# Revit family: is_2360_de_eco_034733
name_source: partatom
category: Elektroinstallationen
revit_build: Autodesk Revit 2016 (Build: 20190508_0715(x64)
units: mm (PartAtom-declared; Revit-internal decimal feet)

## family parameters
Basisbauteil = Fläche
Beim Laden mit Abzugskörper schneiden = Nein
Bemaßung runder Anschluss = Durchmesser verwenden
Beschriftungsausrichtung beibehalten = Nein
Gemeinsam genutzt = Nein
Raumberechnungspunkt = Nein
Teiletyp = Normal

## types (1)
- IS 2360 DE ECO
    Apparent Load = 0 VA
    Beschreibung = Type: Motion detectors; Dimensions (Ø x H): 78 x 84 mm; Mains power supply: 220 – 240 V / 50 – 60 Hz; Sensor Technology: passive infrared; Application, place: Outdoors, Indoors; Application, room: corridor / aisle, changing room, function room / ancillary room, kitchenette, stairwell, WC / washroom, outdoors, front door, all round the building, terrace / balcony, Indoors; Installation site: ceiling; Installation: Installation; Electronic scalability: No; Mechanical scalability: No; Mounting height: 2,2 – 4 m; Optimum mounting height: 2,5 m; Detection angle: 360 °; Angle of aperture: 180 °; Sneak-by guard: Yes; Capability of masking out individual segments: Yes; Reach, radial: Ø 4 m (13 m²); Reach, tangential: Ø 8 m (50 m²); Twilight setting TEACH: No; Twilight setting: 2 – 2000 lx; Time setting: 8 sec – 35 min; Switching output 1, number of LEDs / fluorescent lamps: 6 pcs.; Constant-lighting control: No; Basic light level function: No; Settings via: Potentiometers; Interconnection: No; Type of interconnection: Master/master; IP-rating: IP54; Material: Plastic; Ambient temperature: -20 – 40 °C; Colour: white; Colour, RAL: 9010; IDs, certificates: VDE; Manufacturer's Warranty: 5 years; PU1, EAN: 4007841034733
    Height = 0 mm  [stored 0 ft]
    Hersteller = Steinel
    Length = 78 mm  [stored 0.255906 ft]
    ModVariant = Nein
    Modell = 034733
    Number of Poles = 1
    OnlyDefault = Ja
    Power Factor = 1
    Product Name = IS 2360 DE ECO
    Product group = Sensor-switched indoor light
    ProductGroupID = 30
    Protection Class = Protection class II
    Protection Degree = IP 54
    RlxData = <blob elided: 45549 chars, md5=4ff79cb4>
    SensorDataFile = {"IESDataFiles":[]}
    Typenbild = produkt1_034733.jpg
    Typenkommentare = Product without accessories
    URL = http://relux.com
    VarID = ---
    Voltage = 0 V
    Vorgabe-Ansicht = 1800 mm
    Weight = 0.00 kg
    Width = 0 mm  [stored 0 ft]

note: [stored X ft] marks values corroborated as IEEE doubles in the binary element streams (Revit-internal decimal feet)

## geometry (parser evidence)
native form markers: Blend x4, Sweep x12
no freeform markers — native parametric forms only
